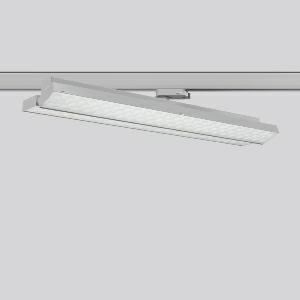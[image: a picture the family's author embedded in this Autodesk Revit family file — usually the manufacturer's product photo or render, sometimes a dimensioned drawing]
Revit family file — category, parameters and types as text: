
# Revit family: tx-move_742161_004_39c3
name_source: partatom
category: Lighting Fixtures
units: mm (PartAtom-declared; Revit-internal decimal feet)

## family parameters
Cut with Voids When Loaded = No
Host = Face
Light Source = No
Part Type = Normal
Room Calculation Point = No
Round Connector Dimension = Use Diameter
Shared = No

## types (1)
- MultiLumen 1 (1 x LED Modul 830, 2900 lm, 3000)
    Apparent Load = 41 VA
    CIE Flux Codes = 90 97 99 100 100
    Color Rendering = 80
    Color Temperature = 3000
    Default Elevation = 1800 mm
    Description = Series: TX-MOVE
Multifunctional surface-mounted spotlight for area lighting. Very flat design. Housing: sheet steel, powder-coated. Rotation range: 356°. Swivel range: 90°. Consistent alignment possible with visible tilt scale. High-efficiency LED units with optimum light control thanks to clear plastic (PC) lens optics. Spezielle Mikrostrukturen reduzieren Gelbsaum. Symmetrical light distribution. With multi adaptor for 3-circuit tracks 230 V. Suitable for Track on ceiling. MultiLumen: Luminous flux adjustable in 3 steps. Factory setting is the highest luminous flux. Environmentally friendly and resource-saving due to replaceable and recyclable components. Very good glare control, ideal for till areas. 
Colour: silver, matt (approx. RAL 9006)
Length: 570 mm
Width: 119 mm
Height: 92 mm
Lamp: LED
Socket: without socket
Colour temperature: 3000K
Colour rendering index (CRI): 80
System power: 41 W
Rated luminous flux: 5800 lm
Luminous efficiency: 141 lm/W
System power 2: 57 W
Rated luminous flux 2: 7850 lm
Luminous efficiency 2: 138 lm/W
System power 3: 73 W
Rated luminous flux 3: 9600 lm
Luminous efficiency 3: 132 lm/W
Control gear: Regulated power supply
Protection class: I
Type of protection: IP 20
    Height = 75 mm
    Lamp = 1 x LED Modul 830
    Lamp Light Flux = 2900 lm
    Lamp count = 1
    Length = 569 mm
    Lifetime = 50000 h
    Luminous efficacy = 141 lm/W
    Manufacturer = RZB
    ModVariant = No
    Model = 742161.004
    Mounting Place = Ceiling
    Mounting Type = Surface mounted
    Number of Poles = 1
    OnlyDefault = Yes
    Power Factor = 1
    Product Name = TX-MOVE
    Product group = Track mounted projectors
    ProductGroupID = 301
    Protection Class = Protection class I
    Protection Degree = IP 20
    RLX_Detail_Level = 1
    RLX_Emergency_Light_Flux = 0 lm
    RLX_Emergency_Type = 0
    RLX_Emergency_Type_DB = No
    RlxData = <blob elided: 33205 chars, md5=072b1673>
    Socket = socket
    Standby Power = 0 W
    System Light Flux = 5800 lm
    System Power = 41 W
    Type Comments = MultiLumen 1
    Type Image = 742162.004.jpg
    URL = http://relux.com
    VarID = multilumen_1
    Voltage = 0 V
    Weight = 0.00 kg
    Width = 119 mm

## geometry (parser evidence)
native form markers: Blend x4, Sweep x13
no freeform markers — native parametric forms only
